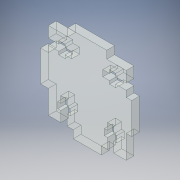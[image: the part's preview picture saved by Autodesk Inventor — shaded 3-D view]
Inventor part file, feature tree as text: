
AUTODESK INVENTOR PART (.ipt)
format: ipt  version: 2019 (Build 230136000, 136)  size: 226,816 bytes
history: native  units: mm
features: extrude x3, sketch x3, projected_geometry x2
ambient origin geometry x8: Origin, YZ Plane, XZ Plane, XY Plane, X Axis, Y Axis, Z Axis, Center Point
bodies: Solid1 (feature_tree)
feature tree (8):
  extrude  "Extrusion1"  Depth=50.0mm
  extrude  "Extrusion2"  Depth=18.0mm
  extrude  "Extrusion3"  Depth=16.0mm
  sketch  "Sketch1"  dims[d0=50.0mm d1=50.0mm]
  sketch  "Sketch2"  dims[d2=5.0mm d3=0.0mm d4=18.0mm]
  projected_geometry  "Projected Loop1"
  sketch  "Sketch3"  dims[d5=5.0mm d6=16.0mm d7=5.0mm d8=20.0mm d9=15.0mm d10=25.0mm d11=12.5mm d12=5.0mm d13=0.0mm d14=3.5mm d15=20.0mm d16=15.0mm d17=15.0mm d18=4.0mm d19=4.0mm d20=8.0mm d21=15.0mm d22=4.0mm d23=4.0mm d24=8.0mm d25=15.0mm d26=4.0mm d27=4.0mm d28=8.0mm d29=8.0mm d30=4.0mm d31=4.0mm d32=15.0mm d33=4.0mm d34=4.0mm d35=8.0mm d36=7.0mm d37=5.0mm d38=0.0mm d39=5.0mm]
  projected_geometry  "Projected Loop2"
